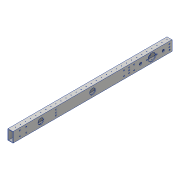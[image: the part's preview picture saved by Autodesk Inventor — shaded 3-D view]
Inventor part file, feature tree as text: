
AUTODESK INVENTOR PART (.ipt)
format: ipt  version: 2018 (Build 220112000, 112)  size: 272,384 bytes
history: native  units: in
note: dims shown in document units (in); Inventor stores cm internally (conversion verified against a paired STEP export)
features: sketch x11, hole x10, reference x9, other x7, projected_geometry x2, extrude x1, shell x1
ambient origin geometry x8: Origin, YZ Plane, XZ Plane, XY Plane, X Axis, Y Axis, Z Axis, Center Point
bodies: Solid1 (feature_tree)
feature tree (41):
  extrude  "Extrusion1"  Depth=2.0in
  shell  "Shell1"  Thickness=31.5in
  hole  "Hole1"  [1 undecoded]
  hole  "Hole2"  [1 undecoded]
  hole  "Hole3"  [1 undecoded]
  hole  "Hole4"  [1 undecoded]
  sketch  "Sketch6"  dims[d23=1.5in d24=0.75in d25=0.375in d26=0.25in d27=0.5635in d28=1.0in d29=0.8108in d30=0.9375in]
  hole  "Hole5"  [1 undecoded]
  hole  "Hole6"  [1 undecoded]
  hole  "Hole7"  [1 undecoded]
  hole  "Hole8"  [1 undecoded]
  hole  "Hole9"  [1 undecoded]
  hole  "Hole10"  [1 undecoded]
  sketch  "Sketch1"  dims[d0=1.0in d1=2.0in d2=31.5in d3=0.0in]
  sketch  "Sketch2"  dims[d4=0.1in d5=0.5in]
  sketch  "Sketch3"  dims[d6=0.5in d7=12.2047in d9=1.0in d10=0.3937in d12=1.0in]
  sketch  "Sketch4"  dims[d14=0.1in d15=0.75in d16=0.375in d17=0.25in d18=0.5635in d19=2.0in d20=0.8108in d21=4.0in]
  projected_geometry  "Projected Loop1"
  sketch  "Sketch5"  dims[d22=1.0in]
  reference  "Reference1"
  reference  "Reference2"
  sketch  "Sketch7"  dims[d31=0.9375in d32=1.0in]
  sketch  "Sketch8"  dims[d33=1.0in]
  reference  "Reference3"
  reference  "Reference4"
  reference  "Reference5"
  reference  "Reference6"
  reference  "Reference7"
  reference  "Reference8"
  sketch  "Sketch9"  dims[d34=0.221in d35=0.75in d36=0.385in d37=0.25in d38=0.5635in d39=1.0in d40=0.8108in]
  reference  "Reference9"
  projected_geometry  "Projected Loop2"
  sketch  "Sketch10"  dims[d41=0.5in d42=0.75in d43=0.385in d44=0.25in d45=0.5635in d46=1.0in d47=0.8108in d48=1.0in]
  sketch  "Sketch11"  dims[d49=1.0in d50=15.75in d51=15.75in d52=5.5in d53=1.125in d54=0.75in d55=0.385in d56=0.25in d57=0.5635in d58=1.0in d59=0.8108in d60=0.375in d61=0.375in d62=0.5in d63=0.5in d64=0.5in d65=0.5in d66=0.375in d67=0.375in d68=0.221in d69=0.75in d70=0.385in d71=0.25in d72=0.5635in d73=1.0in d74=0.8108in d75=0.5in d76=0.5in d77=0.5in d78=0.5in d79=0.5in d80=0.5in d81=0.5in d82=0.5in d83=0.5in d84=0.5in d85=0.5in d86=0.5in d87=0.221in d88=0.75in d89=0.385in d90=0.25in d91=0.5635in d92=1.0in d93=0.8108in d94=0.221in d95=0.75in d96=0.385in d97=0.25in d98=0.5635in d99=1.0in d100=0.8108in d101=0.5in d102=0.5in d103=1.0in d104=1.0in d105=0.221in d106=0.75in d107=0.385in d108=0.25in d109=0.5635in d110=1.0in d111=0.8108in d112=0.221in d113=0.75in d114=0.385in d115=0.25in d116=0.5635in d117=1.0in d118=0.8108in]
  parser-record x1  (decoder bookkeeping rows leaked as tree rows — omitted from the tree; the rows remain in map.json)
  other  "Robot.iam"
  other  "WCP_DS_-_3_CIM_WCD_Base_Kit_w_PTO:2"
  other  "Cross Frame Rail:3"
  other  "Cross Frame Rail:2"
  other  "Drive Frame Rail:2"
  other  "Cross Frame Rail:1"
note: 10 required parameter values undecoded (feature->parameter linkage not recoverable at this tier; creation-order binding heuristic only, values carry confidence <= 0.55)
note: 1 file-system path scrubbed to <path> (originals preserved in map.json)
